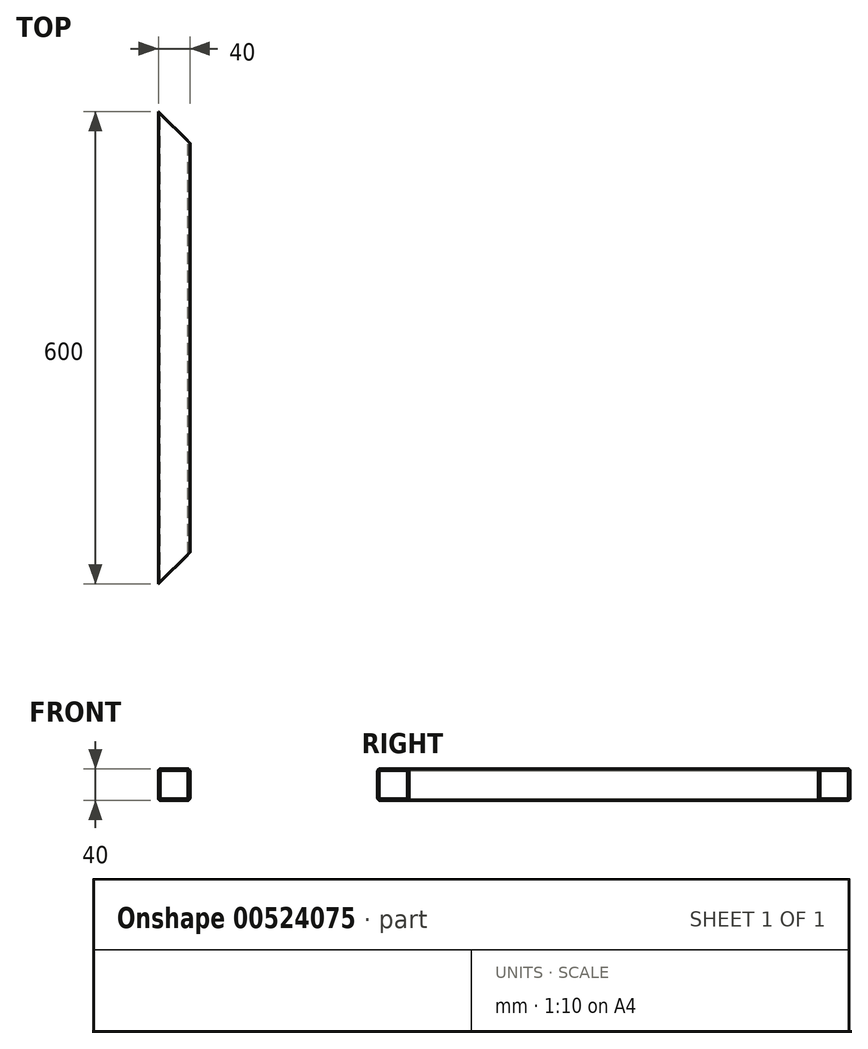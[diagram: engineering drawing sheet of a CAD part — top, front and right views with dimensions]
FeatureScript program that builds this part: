
annotation { "Feature Type Name" : "Feature", "Feature Type Description" : "" }
export const myFeature = defineFeature(function(context is Context, id is Id, definition is map)
    precondition{}
    {
        {
            assignVariable(context, id + "F0", {"name" : "R", "anyValue" : 3});
        }
        {
            assignVariable(context, id + "F1", {"name" : "W", "anyValue" : 2});
        }
        {
            var Q0;
            Q0=qCreatedBy(makeId("Front.planeOp"),FACE);
            var sketch = newSketch(context, id + "F2", { "sketchPlane" : qUnion([Q0])});
            skLineSegment(sketch, "E0.bottom", {"start": v(-20, 20) * mm, "end": v(20, 20) * mm});
            skLineSegment(sketch, "E0.top", {"start": v(-20, -20) * mm, "end": v(20, -20) * mm});
            skLineSegment(sketch, "E0.left", {"start": v(-20, 20) * mm, "end": v(-20, -20) * mm});
            skLineSegment(sketch, "E0.right", {"start": v(20, 20) * mm, "end": v(20, -20) * mm});
            skSolve(sketch);
        }
        {
            var Q0;
            Q0=qSketchRegion(id+"F2",true);
            extrude(context, id + "F3", {"entities" : qUnion([Q0]), "endBound" : BoundingType.SYMMETRIC, "depth" : 600 * mm, "offsetDistance" : 25 * mm});
        }
        {
            var Q0;
            Q0=makeQuery(id+"F3.opExtrude","SWEPT_EDGE",EDGE,{"disambiguationData":[OSD([sQuery(id+"F2.wireOp",EDGE,"E0.bottom"),sQuery(id+"F2.wireOp",EDGE,"E0.right")])]});
            var Q1;
            Q1=makeQuery(id+"F3.opExtrude","SWEPT_EDGE",EDGE,{"disambiguationData":[OSD([sQuery(id+"F2.wireOp",EDGE,"E0.bottom"),sQuery(id+"F2.wireOp",EDGE,"E0.left")])]});
            var Q2;
            Q2=makeQuery(id+"F3.opExtrude","SWEPT_EDGE",EDGE,{"disambiguationData":[OSD([sQuery(id+"F2.wireOp",EDGE,"E0.top"),sQuery(id+"F2.wireOp",EDGE,"E0.right")])]});
            var Q3;
            Q3=makeQuery(id+"F3.opExtrude","SWEPT_EDGE",EDGE,{"disambiguationData":[OSD([sQuery(id+"F2.wireOp",EDGE,"E0.top"),sQuery(id+"F2.wireOp",EDGE,"E0.left")])]});
            fillet(context, id + "F4", {"entities" : qUnion([Q0, Q1, Q2, Q3]), "radius" : (getVariable(context, 'R')) * mm, "tangentPropagation" : true, "allowEdgeOverflow" : false});
        }
        {
            var Q0;
            Q0=makeQuery(id+"F3.opExtrude","CAP_FACE",FACE,{"disambiguationData":[OSD([sQuery(id+"F2.wireOp",EDGE,"E0.bottom"),sQuery(id+"F2.wireOp",EDGE,"E0.top"),sQuery(id+"F2.wireOp",EDGE,"E0.left"),sQuery(id+"F2.wireOp",EDGE,"E0.right")])],"isStart":false});
            var Q1;
            Q1=makeQuery(id+"F3.opExtrude","CAP_FACE",FACE,{"disambiguationData":[OSD([sQuery(id+"F2.wireOp",EDGE,"E0.bottom"),sQuery(id+"F2.wireOp",EDGE,"E0.top"),sQuery(id+"F2.wireOp",EDGE,"E0.left"),sQuery(id+"F2.wireOp",EDGE,"E0.right")])],"isStart":true});
            shell(context, id + "F5", {"entities" : qUnion([Q0, Q1]), "thickness" : (getVariable(context, 'W')) * mm});
        }
        {
            var Q0;
            Q0=makeQuery(id+"F3.opExtrude","SWEPT_FACE",FACE,{"disambiguationData":[OSD([sQuery(id+"F2.wireOp",EDGE,"E0.bottom")])]});
            var sketch = newSketch(context, id + "F6", { "sketchPlane" : qUnion([Q0])});
            skLineSegment(sketch, "E1.0", {"start": v(20, 300) * mm, "end": v(20, -300) * mm, "construction": true});
            skLineSegment(sketch, "E2", {"start": v(20, -260) * mm, "end": v(-20, -300) * mm});
            skLineSegment(sketch, "E3", {"start": v(-20, -300) * mm, "end": v(20, -300) * mm});
            skLineSegment(sketch, "E4", {"start": v(20, -260) * mm, "end": v(20, -300) * mm});
            skPoint(sketch, "E5", {"position": v(0, 300) * mm});
            skLineSegment(sketch, "E6.0", {"start": v(-20, 300) * mm, "end": v(-20, -300) * mm, "construction": true});
            skLineSegment(sketch, "E7", {"start": v(-20, 300) * mm, "end": v(20, 260) * mm});
            skLineSegment(sketch, "E8", {"start": v(20, 260) * mm, "end": v(20, 300) * mm});
            skLineSegment(sketch, "E9", {"start": v(20, 300) * mm, "end": v(-20, 300) * mm});
            skSolve(sketch);
        }
        {
            var Q0;
            Q0=qSketchRegion(id+"F6",true);
            extrude(context, id + "F7", {"entities" : qUnion([Q0]), "operationType" : NewBodyOperationType.REMOVE, "endBound" : BoundingType.THROUGH_ALL, "oppositeDirection" : true, "depth" : 25 * mm, "offsetDistance" : 25 * mm});
        }
    });
